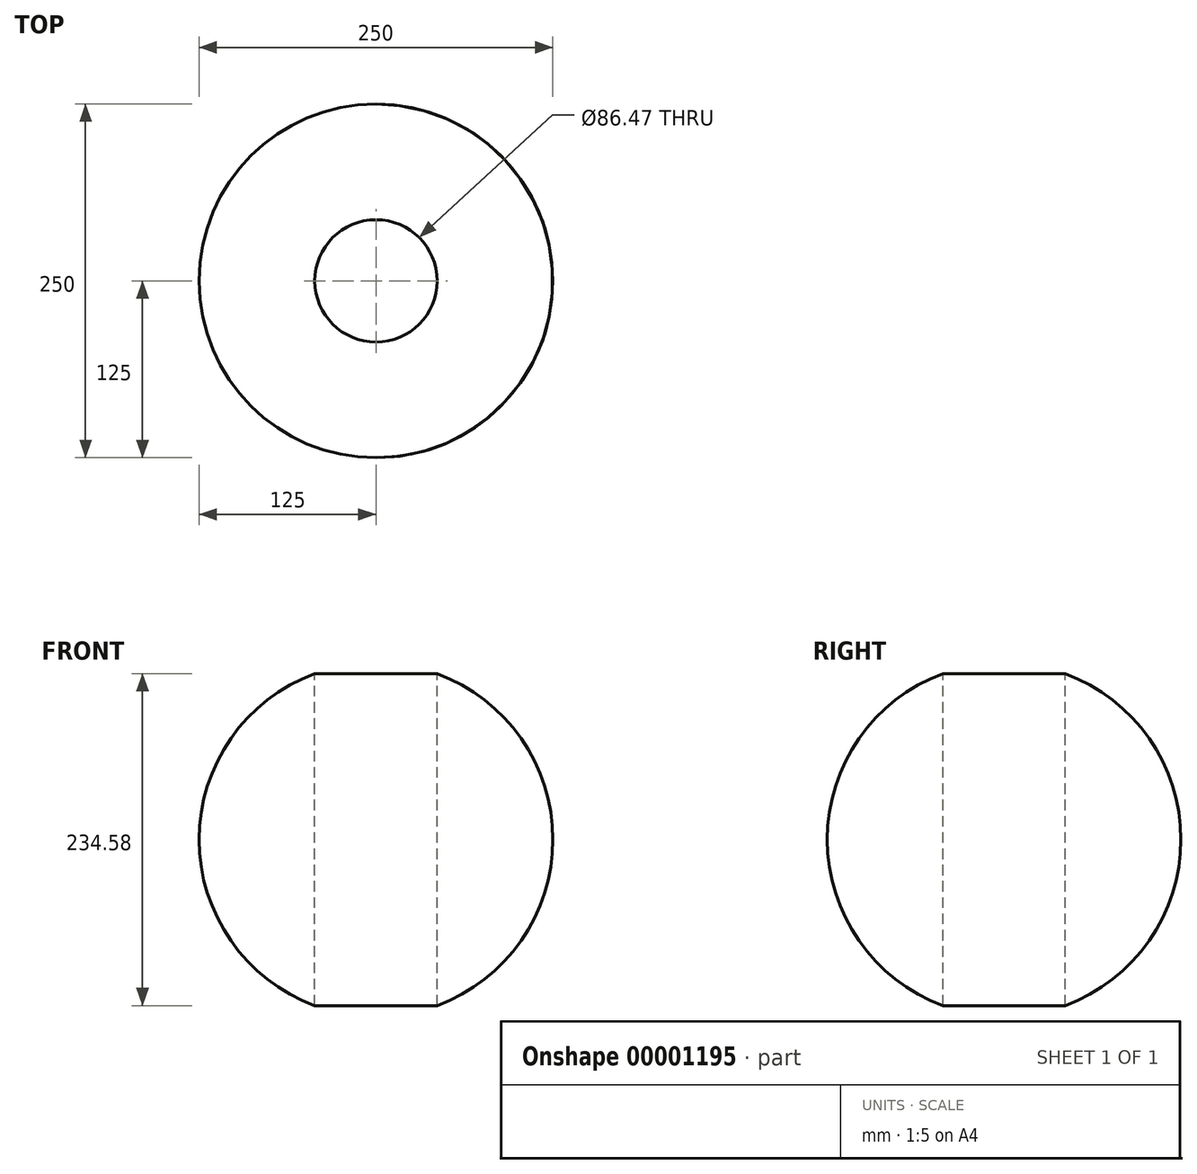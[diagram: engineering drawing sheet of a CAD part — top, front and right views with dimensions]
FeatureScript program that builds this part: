
annotation { "Feature Type Name" : "Feature", "Feature Type Description" : "" }
export const myFeature = defineFeature(function(context is Context, id is Id, definition is map)
    precondition{}
    {
        {
            var Q0;
            Q0=qCreatedBy(makeId("Top.planeOp"),FACE);
            var sketch = newSketch(context, id + "F0", { "sketchPlane" : qUnion([Q0])});
            skCircle(sketch, "E0", {"center": v(0, 0) * mm, "radius": 125 * mm});
            skLineSegment(sketch, "E1", {"start": v(0, 125) * mm, "end": v(0, -125) * mm});
            skSolve(sketch);
        }
        {
            var Q0;
            {var subQ0=sQuery(id+"F0.wireOp",EDGE,"E1");Q0=makeQuery(id+"F0.imprint","IMPRINT",FACE,{"disambiguationData":[TD([[makeQuery(id+"F0.imprint","IMPRINT",EDGE,{"derivedFrom":subQ0}),1.0]])]});}
            var Q1;
            Q1=sQuery(id+"F0.wireOp",EDGE,"E1");
            revolve(context, id + "F1", {"entities" : qUnion([Q0]), "axis" : qUnion([Q1]), "revolveType" : RevolveType.FULL});
        }
        {
            var Q0;
            Q0=qCreatedBy(makeId("Top.planeOp"),FACE);
            var sketch = newSketch(context, id + "F2", { "sketchPlane" : qUnion([Q0])});
            skCircle(sketch, "E2", {"center": v(0, 0) * mm, "radius": 43.23 * mm});
            skSolve(sketch);
        }
        {
            var Q0;
            Q0 = qSketchRegion(id + "F2", true);
            extrude(context, id + "F3", {"entities" : qUnion([Q0]), "operationType" : NewBodyOperationType.REMOVE, "endBound" : BoundingType.SYMMETRIC, "oppositeDirection" : true, "depth" : 712.3 * mm});
        }
    });
